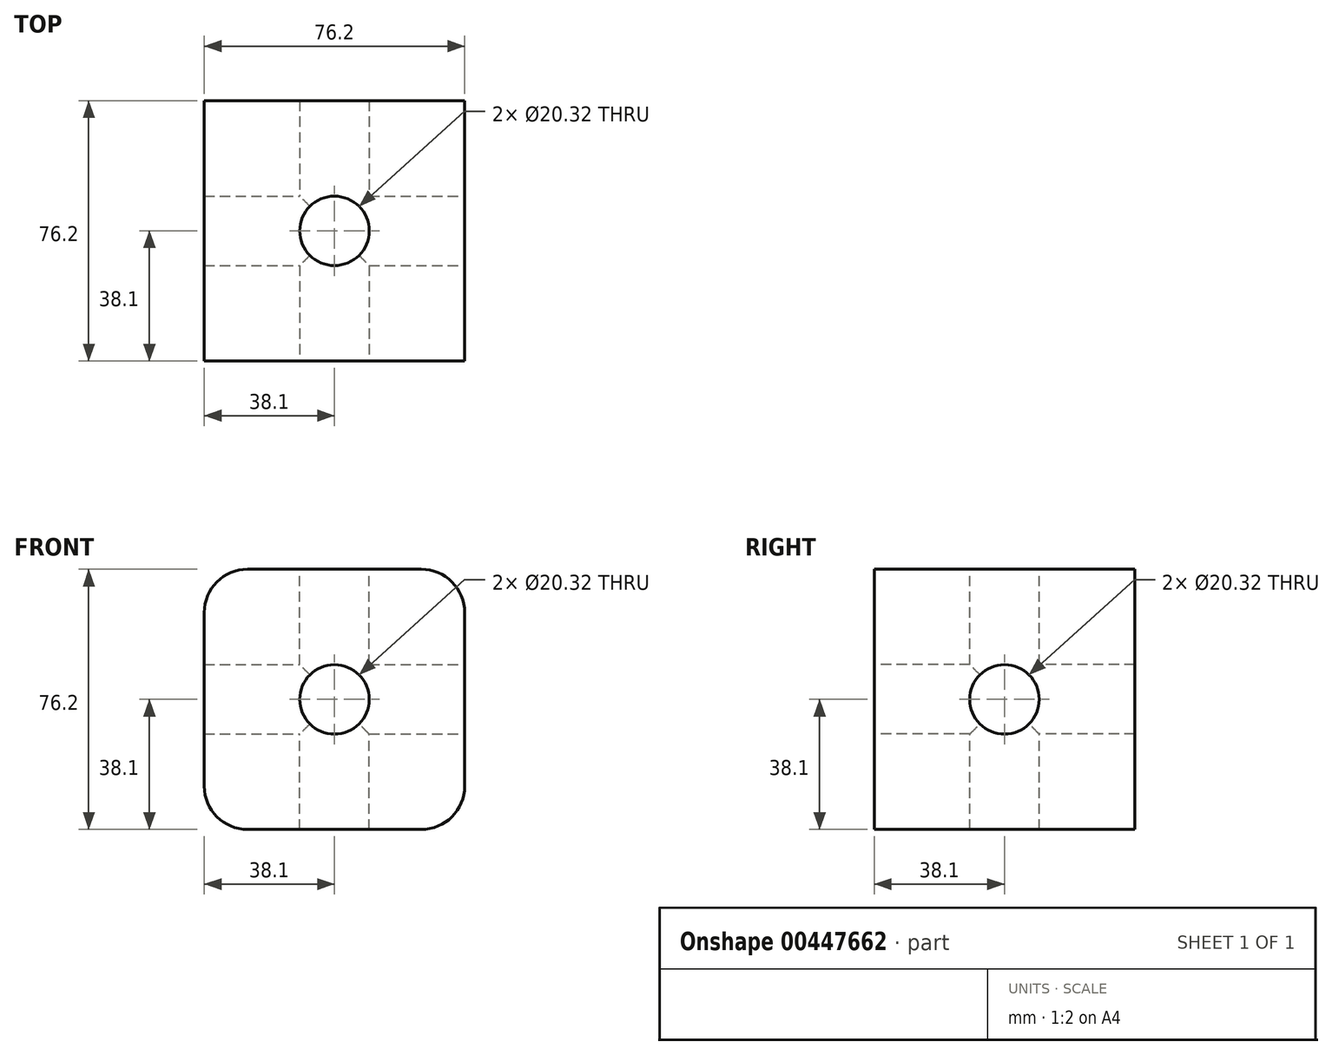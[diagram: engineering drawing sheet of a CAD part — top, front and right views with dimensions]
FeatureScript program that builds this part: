
annotation { "Feature Type Name" : "Feature", "Feature Type Description" : "" }
export const myFeature = defineFeature(function(context is Context, id is Id, definition is map)
    precondition{}
    {
        {
            var Q0;
            Q0=qCreatedBy(makeId("Front.planeOp"),FACE);
            var sketch = newSketch(context, id + "F0", { "sketchPlane" : qUnion([Q0])});
            skLineSegment(sketch, "E0.bottom", {"start": v(0, 0) * mm, "end": v(-76.2, 0) * mm});
            skLineSegment(sketch, "E0.top", {"start": v(0, 76.2) * mm, "end": v(-76.2, 76.2) * mm});
            skLineSegment(sketch, "E0.left", {"start": v(0, 0) * mm, "end": v(0, 76.2) * mm});
            skLineSegment(sketch, "E0.right", {"start": v(-76.2, 0) * mm, "end": v(-76.2, 76.2) * mm});
            skSolve(sketch);
        }
        {
            var Q0;
            Q0=makeQuery(id+"F0.imprint","IMPRINT",FACE,{"disambiguationData":[TD([[makeQuery(id+"F0.imprint","IMPRINT",EDGE,{"derivedFrom":sQuery(id+"F0.wireOp",EDGE,"E0.bottom")}),-1.0]])]});
            extrude(context, id + "F1", {"entities" : qUnion([Q0]), "depth" : 76.2 * mm});
        }
        {
            var Q0;
            Q0=makeQuery(id+"F1.opExtrude","SWEPT_EDGE",EDGE,{"disambiguationData":[OSD([sQuery(id+"F0.wireOp",EDGE,"E0.top"),sQuery(id+"F0.wireOp",EDGE,"E0.left")])]});
            var Q1;
            Q1=makeQuery(id+"F1.opExtrude","SWEPT_EDGE",EDGE,{"disambiguationData":[OSD([sQuery(id+"F0.wireOp",EDGE,"E0.top"),sQuery(id+"F0.wireOp",EDGE,"E0.right")])]});
            var Q2;
            Q2=makeQuery(id+"F1.opExtrude","SWEPT_EDGE",EDGE,{"disambiguationData":[OSD([sQuery(id+"F0.wireOp",EDGE,"E0.bottom"),sQuery(id+"F0.wireOp",EDGE,"E0.left")])]});
            var Q3;
            Q3=makeQuery(id+"F1.opExtrude","SWEPT_EDGE",EDGE,{"disambiguationData":[OSD([sQuery(id+"F0.wireOp",EDGE,"E0.bottom"),sQuery(id+"F0.wireOp",EDGE,"E0.right")])]});
            fillet(context, id + "F2", {"entities" : qUnion([Q0, Q1, Q2, Q3]), "radius" : 12.7 * mm, "tangentPropagation" : true, "allowEdgeOverflow" : false});
        }
        {
            var Q0;
            Q0=makeQuery(id+"F1.opExtrude","CAP_FACE",FACE,{"disambiguationData":[OSD([sQuery(id+"F0.wireOp",EDGE,"E0.bottom"),sQuery(id+"F0.wireOp",EDGE,"E0.top"),sQuery(id+"F0.wireOp",EDGE,"E0.left"),sQuery(id+"F0.wireOp",EDGE,"E0.right")])],"isStart":false});
            var sketch = newSketch(context, id + "F3", { "sketchPlane" : qUnion([Q0])});
            skCircle(sketch, "E1", {"center": v(-38.1, 38.1) * mm, "radius": 10.16 * mm});
            skSolve(sketch);
        }
        {
            var Q0;
            Q0 = qSketchRegion(id + "F3", true);
            extrude(context, id + "F4", {"entities" : qUnion([Q0]), "operationType" : NewBodyOperationType.REMOVE, "endBound" : BoundingType.THROUGH_ALL, "oppositeDirection" : true, "depth" : 25.4 * mm});
        }
        {
            var Q0;
            Q0=makeQuery(id+"F1.opExtrude","SWEPT_FACE",FACE,{"disambiguationData":[OSD([sQuery(id+"F0.wireOp",EDGE,"E0.left")])]});
            var sketch = newSketch(context, id + "F5", { "sketchPlane" : qUnion([Q0])});
            skCircle(sketch, "E2", {"center": v(-38.1, 38.1) * mm, "radius": 10.16 * mm});
            skSolve(sketch);
        }
        {
            var Q0;
            Q0 = qSketchRegion(id + "F5", true);
            extrude(context, id + "F6", {"entities" : qUnion([Q0]), "operationType" : NewBodyOperationType.REMOVE, "endBound" : BoundingType.THROUGH_ALL, "oppositeDirection" : true, "depth" : 25.4 * mm});
        }
        {
            var Q0;
            Q0=makeQuery(id+"F1.opExtrude","SWEPT_FACE",FACE,{"disambiguationData":[OSD([sQuery(id+"F0.wireOp",EDGE,"E0.top")])]});
            var sketch = newSketch(context, id + "F7", { "sketchPlane" : qUnion([Q0])});
            skCircle(sketch, "E3", {"center": v(-38.1, -38.1) * mm, "radius": 10.16 * mm});
            skSolve(sketch);
        }
        {
            var Q0;
            Q0 = qSketchRegion(id + "F7", true);
            extrude(context, id + "F8", {"entities" : qUnion([Q0]), "operationType" : NewBodyOperationType.REMOVE, "endBound" : BoundingType.THROUGH_ALL, "oppositeDirection" : true, "depth" : 25.4 * mm});
        }
    });
